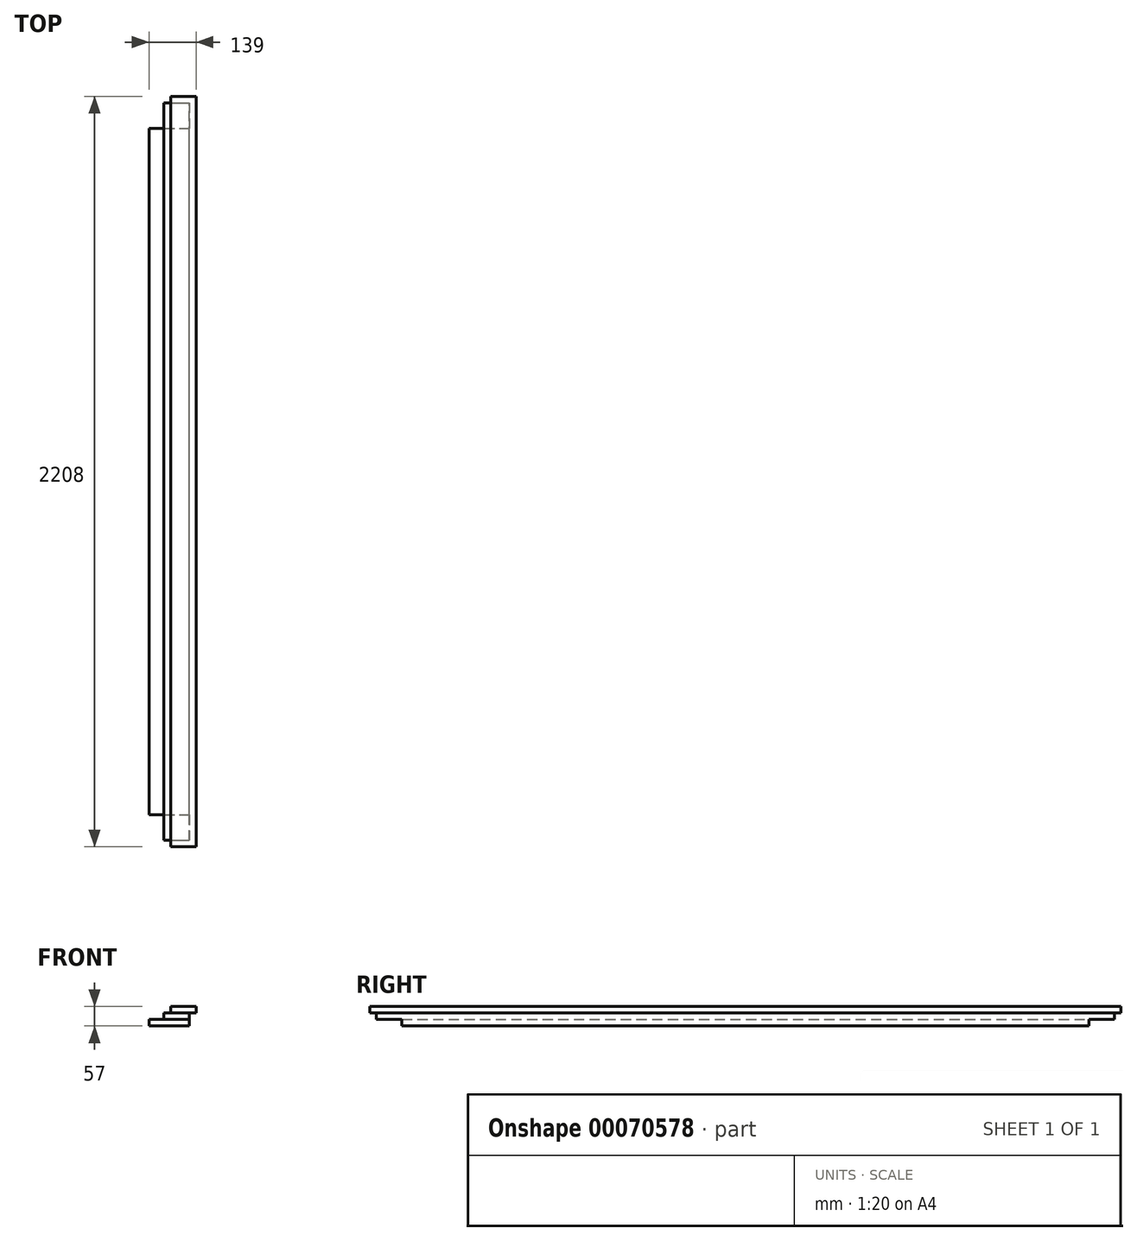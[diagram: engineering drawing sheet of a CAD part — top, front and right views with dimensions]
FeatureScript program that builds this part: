
annotation { "Feature Type Name" : "Feature", "Feature Type Description" : "" }
export const myFeature = defineFeature(function(context is Context, id is Id, definition is map)
    precondition{}
    {
        {
            var Q0;
            Q0=qCreatedBy(makeId("Front.planeOp"),FACE);
            var sketch = newSketch(context, id + "F0", { "sketchPlane" : qUnion([Q0])});
            skLineSegment(sketch, "E0", {"start": v(0, 0) * mm, "end": v(-75, 0) * mm});
            skLineSegment(sketch, "E1", {"start": v(-75, 0) * mm, "end": v(-75, -19) * mm});
            skLineSegment(sketch, "E2", {"start": v(-75, -19) * mm, "end": v(-95, -19) * mm});
            skLineSegment(sketch, "E3", {"start": v(-95, -19) * mm, "end": v(-95, -38) * mm});
            skLineSegment(sketch, "E4", {"start": v(-95, -38) * mm, "end": v(-139, -38) * mm});
            skLineSegment(sketch, "E5", {"start": v(-139, -38) * mm, "end": v(-139, -57) * mm});
            skLineSegment(sketch, "E6", {"start": v(-139, -57) * mm, "end": v(-20, -57) * mm});
            skLineSegment(sketch, "E7", {"start": v(-20, -57) * mm, "end": v(-20, -19) * mm});
            skLineSegment(sketch, "E8", {"start": v(-20, -19) * mm, "end": v(0, -19) * mm});
            skLineSegment(sketch, "E9", {"start": v(0, -19) * mm, "end": v(0, 0) * mm});
            skSolve(sketch);
        }
        {
            var Q0;
            Q0 = qSketchRegion(id + "F0", true);
            extrude(context, id + "F1", {"entities" : qUnion([Q0]), "endBound" : BoundingType.SYMMETRIC, "depth" : 2208 * mm});
        }
        {
            var Q0;
            Q0=makeQuery(id+"F1.opExtrude","SWEPT_FACE",FACE,{"disambiguationData":[OSD([sQuery(id+"F0.wireOp",EDGE,"E6")])]});
            var sketch = newSketch(context, id + "F2", { "sketchPlane" : qUnion([Q0])});
            skLineSegment(sketch, "E10.bottom", {"start": v(-139, 1104) * mm, "end": v(54.68, 1104) * mm});
            skLineSegment(sketch, "E10.top", {"start": v(-139, 1010) * mm, "end": v(54.68, 1010) * mm});
            skLineSegment(sketch, "E10.left", {"start": v(-139, 1104) * mm, "end": v(-139, 1010) * mm});
            skLineSegment(sketch, "E10.right", {"start": v(54.68, 1104) * mm, "end": v(54.68, 1010) * mm});
            skLineSegment(sketch, "E11.bottom", {"start": v(-139, -1104) * mm, "end": v(68, -1104) * mm});
            skLineSegment(sketch, "E11.top", {"start": v(-139, -1010) * mm, "end": v(68, -1010) * mm});
            skLineSegment(sketch, "E11.left", {"start": v(-139, -1104) * mm, "end": v(-139, -1010) * mm});
            skLineSegment(sketch, "E11.right", {"start": v(68, -1104) * mm, "end": v(68, -1010) * mm});
            skSolve(sketch);
        }
        {
            var Q0;
            Q0 = qSketchRegion(id + "F2", true);
            extrude(context, id + "F3", {"entities" : qUnion([Q0]), "operationType" : NewBodyOperationType.REMOVE, "oppositeDirection" : true, "depth" : 19 * mm});
        }
        {
            var Q0;
            Q0=makeQuery(id+"F3.boolean.opBoolean","COPY",FACE,{"derivedFrom":makeQuery(id+"F3.opExtrude","CAP_FACE",FACE,{"disambiguationData":[OSD([sQuery(id+"F2.wireOp",EDGE,"E10.bottom"),sQuery(id+"F2.wireOp",EDGE,"E10.top"),sQuery(id+"F2.wireOp",EDGE,"E10.left"),sQuery(id+"F2.wireOp",EDGE,"E10.right")])],"isStart":false})});
            var sketch = newSketch(context, id + "F4", { "sketchPlane" : qUnion([Q0])});
            skLineSegment(sketch, "E12.bottom", {"start": v(-95, 1104) * mm, "end": v(-20, 1104) * mm});
            skLineSegment(sketch, "E12.top", {"start": v(-95, 1085) * mm, "end": v(-20, 1085) * mm});
            skLineSegment(sketch, "E12.left", {"start": v(-95, 1104) * mm, "end": v(-95, 1085) * mm});
            skLineSegment(sketch, "E12.right", {"start": v(-20, 1104) * mm, "end": v(-20, 1085) * mm});
            skLineSegment(sketch, "E13.bottom", {"start": v(-95, -1104) * mm, "end": v(-20, -1104) * mm});
            skLineSegment(sketch, "E13.top", {"start": v(-95, -1085) * mm, "end": v(-20, -1085) * mm});
            skLineSegment(sketch, "E13.left", {"start": v(-95, -1104) * mm, "end": v(-95, -1085) * mm});
            skLineSegment(sketch, "E13.right", {"start": v(-20, -1104) * mm, "end": v(-20, -1085) * mm});
            skSolve(sketch);
        }
        {
            var Q0;
            Q0 = qSketchRegion(id + "F4", true);
            extrude(context, id + "F5", {"entities" : qUnion([Q0]), "operationType" : NewBodyOperationType.REMOVE, "oppositeDirection" : true, "depth" : 19 * mm});
        }
    });
